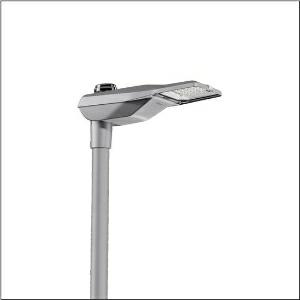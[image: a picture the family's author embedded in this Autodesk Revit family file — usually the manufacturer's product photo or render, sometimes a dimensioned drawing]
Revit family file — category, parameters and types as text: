
# Revit family: streetlight_sl_21_micro___st1_5a_5xe5p37n08cb_e60d
name_source: partatom
category: Lighting Fixtures
units: mm (PartAtom-declared; Revit-internal decimal feet)

## family parameters
Cut with Voids When Loaded = No
Host = Face
Light Source = No
Part Type = Normal
Room Calculation Point = No
Round Connector Dimension = Use Diameter
Shared = No

## types (1)
- --- (1 x LED, 2250 lm, 15.8 W, 3000K)
    Apparent Load = 16 VA
    CIE Flux Codes = 22 53 95 100 100
    Color Rendering = 70
    Color Temperature = 3000K
    Default Elevation = 1800 mm
    Description = Streetlight SL 21 micro, mast luminaire, primary light control with lens, of PMMA, primary optical cover: cover, of toughened safety glass, transparent, light distribution: ST1.5a, light emission: direct distribution, primary light characteristic: asymmetric, installation type: post-top, LED, 3G 1.5mm², High Power LED, rated luminous flux: 2.250lm, luminous efficacy: 142lm/W, light colour: 730, colour temperature: 3000K, control gear: NEMA (7pin), control: overheat protection, pre-setting: linear dimming characteristic, constant luminous flux control, time-dependent luminous flux control, flexible luminous flux parameterisation, mains connection: 230..240V, AC, 50/60Hz, connection cable pre-assembled, cable length: 6,5m, wiring characteristics: H07RN-F, start of lifetime: 16W, end of service life: 16W, reduction: 8W, luminaire housing, of diecast aluminium (EN AC-44300), powder-coated, Siteco® metallic grey (DB 702S), corrosivity category C5 mid according to DIN EN ISO 12944, multi-level sealing system, sealing non-destructively replaceable, inclination adjustable: 0°, 5°, 10°, 15°, length: 528mm, width: 235mm, height: 110mm, spigot size: 76/60mm (post-top), mounting height: 4..8m, protection rating (complete): IP66, insulation class (complete): insulation class I (protective earthing), certification: CE, ENEC, ENEC+, VDE, impact resistance: IK10, permissible operating ambient temperature for outdoor applications: -40..+50°C, standard-compliant lighting for roads and squares, packaging unit: 1 piece

Light Distribution: ST1.5a
    Height = 110 mm
    Lamp = 1 x LED
    Lamp Light Flux = 2250 lm
    Lamp Power = 15.8 W
    Lamp count = 1
    Length = 528 mm
    Luminous efficacy = 142 lm/W
    Manufacturer = Siteco
    ModVariant = No
    Model = 5XE5P37N08CB
    Number of Poles = 1
    OnlyDefault = Yes
    Power Factor = 1
    Product Name = Streetlight SL 21 micro | ST1.5a
    Product group = mast luminaire | pylon top
    ProductGroupID = 6100
    Protection Class = Protection class I
    Protection Degree = IP 66
    RLX_Detail_Level = 1
    RLX_Emergency_Light_Flux = 0 lm
    RLX_Emergency_Type = 0
    RLX_Emergency_Type_DB = No
    RlxData = <blob elided: 101945 chars, md5=29a44f7d>
    Socket = socket
    Standby Power = 0 W
    System Light Flux = 2250 lm
    System Power = 16 W
    Type Comments = factory setting: luminous flux: 100 % | dim-lin: 254 | 300 mA
    Type Image = l_1294375.jpg
    URL = http://relux.com
    VarID = @adj_155283
    Voltage = 0 V
    Weight = 0.00 kg
    Width = 235 mm

## geometry (parser evidence)
native form markers: Blend x4, Sweep x9
no freeform markers — native parametric forms only
